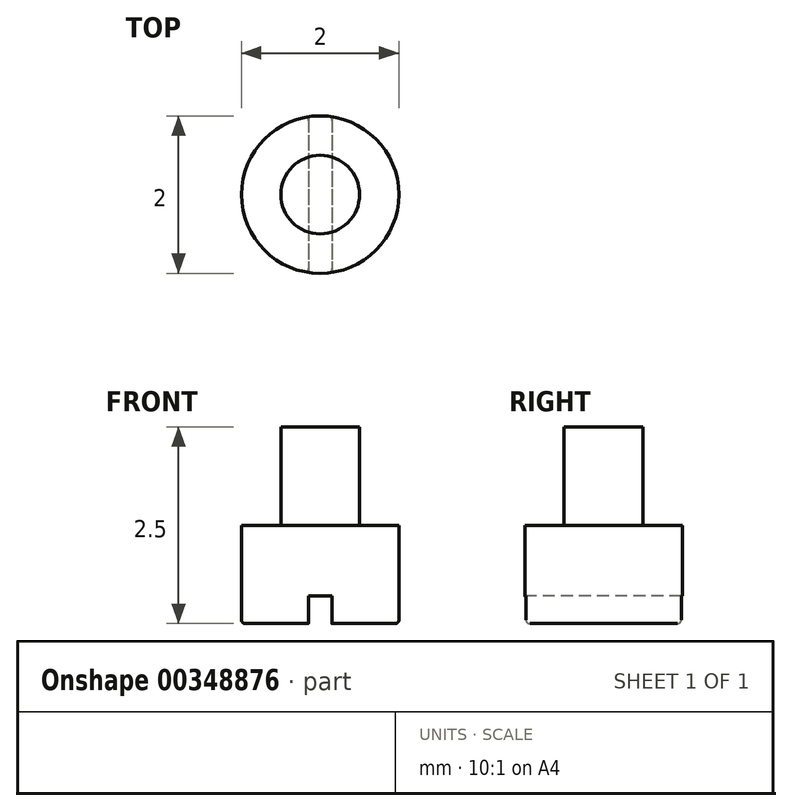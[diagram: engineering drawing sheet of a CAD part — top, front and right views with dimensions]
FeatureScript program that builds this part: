
annotation { "Feature Type Name" : "Feature", "Feature Type Description" : "" }
export const myFeature = defineFeature(function(context is Context, id is Id, definition is map)
    precondition{}
    {
        {
            var Q0;
            Q0=qCreatedBy(makeId("Front.planeOp"),FACE);
            var sketch = newSketch(context, id + "F0", { "sketchPlane" : qUnion([Q0])});
            skLineSegment(sketch, "E0", {"start": v(0, 0) * mm, "end": v(1, 0) * mm});
            skLineSegment(sketch, "E1", {"start": v(1, 0) * mm, "end": v(1, 1.25) * mm});
            skLineSegment(sketch, "E2", {"start": v(1, 1.25) * mm, "end": v(0.5, 1.25) * mm});
            skLineSegment(sketch, "E3", {"start": v(0.5, 1.25) * mm, "end": v(0.5, 2.5) * mm});
            skLineSegment(sketch, "E4", {"start": v(0.5, 2.5) * mm, "end": v(0, 2.5) * mm});
            skLineSegment(sketch, "E5", {"start": v(0, 2.5) * mm, "end": v(0, 0) * mm});
            skSolve(sketch);
        }
        {
            var Q0;
            Q0=qSketchRegion(id+"F0",true);
            var Q1;
            Q1=sQuery(id+"F0.wireOp",EDGE,"E5");
            revolve(context, id + "F1", {"entities" : qUnion([Q0]), "axis" : qUnion([Q1]), "revolveType" : RevolveType.FULL});
        }
        {
            var Q0;
            Q0=makeQuery(id+"F1.opRevolve","SWEPT_EDGE",EDGE,{"disambiguationData":[OSD([sQuery(id+"F0.wireOp",EDGE,"E0"),sQuery(id+"F0.wireOp",EDGE,"E1")])]});
            fillet(context, id + "F2", {"entities" : qUnion([Q0]), "radius" : 0.05 * mm, "tangentPropagation" : true, "allowEdgeOverflow" : false});
        }
        {
            var Q0;
            Q0=qCreatedBy(makeId("Front.planeOp"),FACE);
            var sketch = newSketch(context, id + "F3", { "sketchPlane" : qUnion([Q0])});
            skLineSegment(sketch, "E6", {"start": v(0, 0) * mm, "end": v(0, 0.93) * mm, "construction": true});
            skLineSegment(sketch, "E7.bottom", {"start": v(-0.15, 0.35) * mm, "end": v(0.15, 0.35) * mm});
            skLineSegment(sketch, "E7.top", {"start": v(-0.15, 0) * mm, "end": v(0.15, 0) * mm});
            skLineSegment(sketch, "E7.left", {"start": v(-0.15, 0.35) * mm, "end": v(-0.15, 0) * mm});
            skLineSegment(sketch, "E7.right", {"start": v(0.15, 0.35) * mm, "end": v(0.15, 0) * mm});
            skSolve(sketch);
        }
        {
            var Q0;
            Q0=qSketchRegion(id+"F3",true);
            extrude(context, id + "F4", {"entities" : qUnion([Q0]), "operationType" : NewBodyOperationType.REMOVE, "endBound" : BoundingType.SYMMETRIC, "oppositeDirection" : true, "depth" : 25 * mm});
        }
    });
